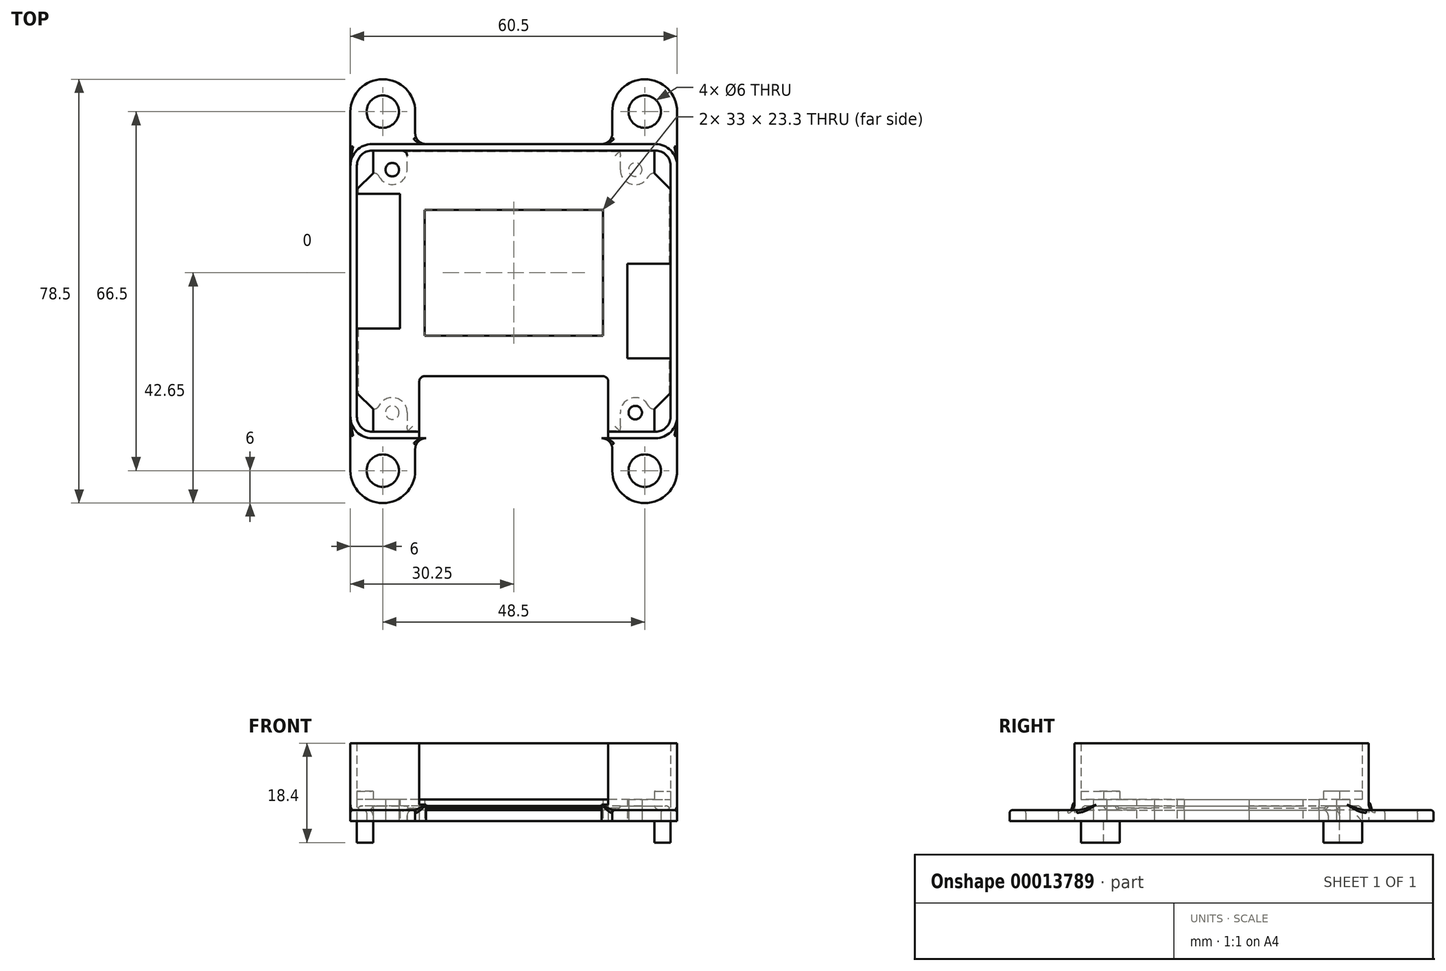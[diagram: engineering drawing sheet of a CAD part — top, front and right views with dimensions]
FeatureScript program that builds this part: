
annotation { "Feature Type Name" : "Feature", "Feature Type Description" : "" }
export const myFeature = defineFeature(function(context is Context, id is Id, definition is map)
    precondition{}
    {
        {
            var Q0;
            Q0=qCreatedBy(makeId("Top.planeOp"),FACE);
            var sketch = newSketch(context, id + "F0", { "sketchPlane" : qUnion([Q0])});
            skLineSegment(sketch, "E0.rect.bottom", {"start": v(26.25, 27.25) * mm, "end": v(-26.25, 27.25) * mm});
            skLineSegment(sketch, "E0.rect.top", {"start": v(26.25, -27.25) * mm, "end": v(-26.25, -27.25) * mm});
            skLineSegment(sketch, "E0.rect.left", {"start": v(30.25, 33.25) * mm, "end": v(30.25, 23.25) * mm});
            skLineSegment(sketch, "E0.rect.right", {"start": v(-30.25, 23.25) * mm, "end": v(-30.25, -23.25) * mm});
            skPoint(sketch, "E0.rect.middle", {"position": v(0, 0) * mm});
            skCircle(sketch, "E1", {"center": v(24.25, 33.25) * mm, "radius": 3 * mm});
            skArc(sketch, "E2.0", {"start": v(30.25, 33.25) * mm, "mid": v(24.25, 39.25) * mm, "end": v(18.25, 33.25) * mm});
            skPoint(sketch, "E3.visualSharp", {"position": v(30.25, 27.25) * mm});
            skArc(sketch, "E3.filletArc", {"start": v(30.25, 23.25) * mm, "mid": v(29.08, 26.08) * mm, "end": v(26.25, 27.25) * mm});
            skPoint(sketch, "E4.visualSharp", {"position": v(-30.25, 27.25) * mm});
            skArc(sketch, "E4.filletArc", {"start": v(-26.25, 27.25) * mm, "mid": v(-29.08, 26.08) * mm, "end": v(-30.25, 23.25) * mm});
            skPoint(sketch, "E5.visualSharp", {"position": v(30.25, -27.25) * mm});
            skArc(sketch, "E5.filletArc", {"start": v(26.25, -27.25) * mm, "mid": v(29.08, -26.08) * mm, "end": v(30.25, -23.25) * mm});
            skPoint(sketch, "E6.visualSharp", {"position": v(-30.25, -27.25) * mm});
            skArc(sketch, "E6.filletArc", {"start": v(-30.25, -23.25) * mm, "mid": v(-29.08, -26.08) * mm, "end": v(-26.25, -27.25) * mm});
            skLineSegment(sketch, "E7", {"start": v(18.25, 33.25) * mm, "end": v(18.25, 27.25) * mm});
            skLineSegment(sketch, "E8", {"start": v(0, 27.25) * mm, "end": v(0, -27.25) * mm, "construction": true});
            skLineSegment(sketch, "E9", {"start": v(-30.25, 0) * mm, "end": v(30.25, 0) * mm, "construction": true});
            skLineSegment(sketch, "E10", {"start": v(30.25, 23.25) * mm, "end": v(30.25, -23.25) * mm});
            skArc(sketch, "E11.0", {"start": v(29.05, 23.25) * mm, "mid": v(28.23, 25.23) * mm, "end": v(26.25, 26.05) * mm});
            skLineSegment(sketch, "E11.1", {"start": v(29.05, 23.25) * mm, "end": v(29.05, -23.25) * mm});
            skArc(sketch, "E11.2", {"start": v(26.25, -26.05) * mm, "mid": v(28.23, -25.23) * mm, "end": v(29.05, -23.25) * mm});
            skLineSegment(sketch, "E11.3", {"start": v(26.25, -26.05) * mm, "end": v(-26.25, -26.05) * mm});
            skArc(sketch, "E11.4", {"start": v(-29.05, -23.25) * mm, "mid": v(-28.23, -25.23) * mm, "end": v(-26.25, -26.05) * mm});
            skLineSegment(sketch, "E11.5", {"start": v(26.25, 26.05) * mm, "end": v(-26.25, 26.05) * mm});
            skLineSegment(sketch, "E11.6", {"start": v(-29.05, 23.25) * mm, "end": v(-29.05, -23.25) * mm});
            skArc(sketch, "E11.7", {"start": v(-26.25, 26.05) * mm, "mid": v(-28.23, 25.23) * mm, "end": v(-29.05, 23.25) * mm});
            skCircle(sketch, "E12", {"center": v(22.5, 22.5) * mm, "radius": 1.25 * mm});
            skArc(sketch, "E13.0", {"start": v(19.75, 22.5) * mm, "mid": v(21.87, 19.82) * mm, "end": v(24.97, 21.28) * mm});
            skLineSegment(sketch, "E14.0.MirrorCS", {"start": v(-18.25, 33.25) * mm, "end": v(-18.25, 27.25) * mm});
            skArc(sketch, "E15.0.MirrorC", {"start": v(-30.25, 33.25) * mm, "mid": v(-24.25, 39.25) * mm, "end": v(-18.25, 33.25) * mm});
            skCircle(sketch, "E16.0.MirrorC", {"center": v(-24.25, 33.25) * mm, "radius": 3 * mm});
            skLineSegment(sketch, "E17.0.MirrorCS", {"start": v(-30.25, 33.25) * mm, "end": v(-30.25, 23.25) * mm});
            skLineSegment(sketch, "E18.0.MirrorCS", {"start": v(-30.25, -33.25) * mm, "end": v(-30.25, -23.25) * mm});
            skLineSegment(sketch, "E19.0.MirrorCS", {"start": v(-18.25, -33.25) * mm, "end": v(-18.25, -27.25) * mm});
            skArc(sketch, "E20.0.MirrorC", {"start": v(-30.25, -33.25) * mm, "mid": v(-24.25, -39.25) * mm, "end": v(-18.25, -33.25) * mm});
            skCircle(sketch, "E21.0.MirrorC", {"center": v(-24.25, -33.25) * mm, "radius": 3 * mm});
            skLineSegment(sketch, "E22.0.MirrorCS", {"start": v(18.25, -33.25) * mm, "end": v(18.25, -27.25) * mm});
            skLineSegment(sketch, "E23.0.MirrorCS", {"start": v(30.25, -33.25) * mm, "end": v(30.25, -23.25) * mm});
            skArc(sketch, "E24.0.MirrorC", {"start": v(30.25, -33.25) * mm, "mid": v(24.25, -39.25) * mm, "end": v(18.25, -33.25) * mm});
            skCircle(sketch, "E25.0.MirrorC", {"center": v(24.25, -33.25) * mm, "radius": 3 * mm});
            skLineSegment(sketch, "E26", {"start": v(26.05, 26.05) * mm, "end": v(26.05, 21.84) * mm});
            skLineSegment(sketch, "E27", {"start": v(26.05, 21.84) * mm, "end": v(29.05, 18.84) * mm});
            skLineSegment(sketch, "E28", {"start": v(19.75, 22.5) * mm, "end": v(19.75, 26.05) * mm});
            skCircle(sketch, "E29.0.MirrorC", {"center": v(-22.5, 22.5) * mm, "radius": 1.25 * mm});
            skLineSegment(sketch, "E30", {"start": v(26.05, 21.84) * mm, "end": v(25.86, 21.84) * mm});
            skPoint(sketch, "E31.visualSharp", {"position": v(25.17, 21.84) * mm});
            skArc(sketch, "E31.filletArc", {"start": v(25.86, 21.84) * mm, "mid": v(25.33, 21.69) * mm, "end": v(24.97, 21.28) * mm});
            skLineSegment(sketch, "E32.0.MirrorCS", {"start": v(-19.75, 22.5) * mm, "end": v(-19.75, 26.05) * mm});
            skArc(sketch, "E33.0.MirrorCS", {"start": v(-19.75, 22.5) * mm, "mid": v(-21.87, 19.82) * mm, "end": v(-24.97, 21.28) * mm});
            skArc(sketch, "E34.0.MirrorCS", {"start": v(-25.86, 21.84) * mm, "mid": v(-25.33, 21.69) * mm, "end": v(-24.97, 21.28) * mm});
            skLineSegment(sketch, "E35.0.MirrorCS", {"start": v(-26.05, 21.84) * mm, "end": v(-25.86, 21.84) * mm});
            skLineSegment(sketch, "E36.0.MirrorCS", {"start": v(-26.05, 21.84) * mm, "end": v(-29.05, 18.84) * mm});
            skLineSegment(sketch, "E37.0.MirrorCS", {"start": v(-26.05, 26.05) * mm, "end": v(-26.05, 21.84) * mm});
            skLineSegment(sketch, "E38.0.MirrorCS", {"start": v(26.05, -21.84) * mm, "end": v(25.86, -21.84) * mm});
            skArc(sketch, "E38.1.MirrorCS", {"start": v(25.86, -21.84) * mm, "mid": v(25.33, -21.69) * mm, "end": v(24.97, -21.28) * mm});
            skLineSegment(sketch, "E38.2.MirrorCS", {"start": v(26.05, -21.84) * mm, "end": v(29.05, -18.84) * mm});
            skArc(sketch, "E38.3.MirrorCS", {"start": v(19.75, -22.5) * mm, "mid": v(21.87, -19.82) * mm, "end": v(24.97, -21.28) * mm});
            skLineSegment(sketch, "E38.4.MirrorCS", {"start": v(19.75, -22.5) * mm, "end": v(19.75, -26.05) * mm});
            skLineSegment(sketch, "E38.5.MirrorCS", {"start": v(26.05, -26.05) * mm, "end": v(26.05, -21.84) * mm});
            skCircle(sketch, "E38.6.MirrorC", {"center": v(22.5, -22.5) * mm, "radius": 1.25 * mm});
            skLineSegment(sketch, "E38.7.MirrorCS", {"start": v(-26.05, -21.84) * mm, "end": v(-25.86, -21.84) * mm});
            skArc(sketch, "E38.8.MirrorCS", {"start": v(-25.86, -21.84) * mm, "mid": v(-25.33, -21.69) * mm, "end": v(-24.97, -21.28) * mm});
            skArc(sketch, "E38.9.MirrorCS", {"start": v(-19.75, -22.5) * mm, "mid": v(-21.87, -19.82) * mm, "end": v(-24.97, -21.28) * mm});
            skLineSegment(sketch, "E38.10.MirrorCS", {"start": v(-26.05, -21.84) * mm, "end": v(-29.05, -18.84) * mm});
            skLineSegment(sketch, "E38.12.MirrorCS", {"start": v(-26.05, -26.05) * mm, "end": v(-26.05, -21.84) * mm});
            skLineSegment(sketch, "E38.13.MirrorCS", {"start": v(-19.75, -22.5) * mm, "end": v(-19.75, -26.05) * mm});
            skCircle(sketch, "E39.0.MirrorC", {"center": v(-22.5, -22.5) * mm, "radius": 1.25 * mm});
            skSolve(sketch);
        }
        {
            var Q0;
            {var subQ1=sQuery(id+"F0.wireOp",EDGE,"E4.filletArc");Q0=makeQuery(id+"F0.imprint","IMPRINT",FACE,{"disambiguationData":[TD([[makeQuery(id+"F0.imprint","IMPRINT",EDGE,{"derivedFrom":subQ1}),-1.0]])]});}
            var Q1;
            {var subQ1=sQuery(id+"F0.wireOp",EDGE,"E4.filletArc");Q1=makeQuery(id+"F0.imprint","IMPRINT",FACE,{"disambiguationData":[TD([[makeQuery(id+"F0.imprint","IMPRINT",EDGE,{"derivedFrom":subQ1}),-1.0]])]});}
            var Q2;
            {var subQ1=sQuery(id+"F0.wireOp",EDGE,"E4.filletArc");Q2=makeQuery(id+"F0.imprint","IMPRINT",FACE,{"disambiguationData":[TD([[makeQuery(id+"F0.imprint","IMPRINT",EDGE,{"derivedFrom":subQ1}),-1.0]])]});}
            var Q3;
            Q3=makeQuery(id+"F0.imprint","IMPRINT",FACE,{"disambiguationData":[TD([[makeQuery(id+"F0.imprint","IMPRINT",EDGE,{"derivedFrom":sQuery(id+"F0.wireOp",EDGE,"E0.rect.left")}),-1.0]])]});
            var Q4;
            Q4=makeQuery(id+"F0.imprint","IMPRINT",FACE,{"disambiguationData":[TD([[makeQuery(id+"F0.imprint","IMPRINT",EDGE,{"derivedFrom":sQuery(id+"F0.wireOp",EDGE,"E0.rect.left")}),-1.0]])]});
            var Q5;
            Q5=makeQuery(id+"F0.imprint","IMPRINT",FACE,{"disambiguationData":[TD([[makeQuery(id+"F0.imprint","IMPRINT",EDGE,{"derivedFrom":sQuery(id+"F0.wireOp",EDGE,"E0.rect.left")}),-1.0]])]});
            var Q6;
            Q6=makeQuery(id+"F0.imprint","IMPRINT",FACE,{"disambiguationData":[TD([[makeQuery(id+"F0.imprint","IMPRINT",EDGE,{"derivedFrom":sQuery(id+"F0.wireOp",EDGE,"E0.rect.right")}),1.0]])]});
            var Q7;
            {var subQ3=sQuery(id+"F0.wireOp",EDGE,"E11.0");Q7=makeQuery(id+"F0.imprint","IMPRINT",FACE,{"disambiguationData":[TD([[makeQuery(id+"F0.imprint","IMPRINT",EDGE,{"derivedFrom":subQ3}),1.0]])]});}
            var Q8;
            {var subQ1=sQuery(id+"F0.wireOp",EDGE,"E5.filletArc");Q8=makeQuery(id+"F0.imprint","IMPRINT",FACE,{"disambiguationData":[TD([[makeQuery(id+"F0.imprint","IMPRINT",EDGE,{"derivedFrom":subQ1}),-1.0]])]});}
            var Q9;
            {var subQ1=sQuery(id+"F0.wireOp",EDGE,"E5.filletArc");Q9=makeQuery(id+"F0.imprint","IMPRINT",FACE,{"disambiguationData":[TD([[makeQuery(id+"F0.imprint","IMPRINT",EDGE,{"derivedFrom":subQ1}),-1.0]])]});}
            var Q10;
            {var subQ1=sQuery(id+"F0.wireOp",EDGE,"E5.filletArc");Q10=makeQuery(id+"F0.imprint","IMPRINT",FACE,{"disambiguationData":[TD([[makeQuery(id+"F0.imprint","IMPRINT",EDGE,{"derivedFrom":subQ1}),-1.0]])]});}
            var Q11;
            {var subQ1=sQuery(id+"F0.wireOp",EDGE,"E6.filletArc");Q11=makeQuery(id+"F0.imprint","IMPRINT",FACE,{"disambiguationData":[TD([[makeQuery(id+"F0.imprint","IMPRINT",EDGE,{"derivedFrom":subQ1}),-1.0]])]});}
            var Q12;
            {var subQ1=sQuery(id+"F0.wireOp",EDGE,"E6.filletArc");Q12=makeQuery(id+"F0.imprint","IMPRINT",FACE,{"disambiguationData":[TD([[makeQuery(id+"F0.imprint","IMPRINT",EDGE,{"derivedFrom":subQ1}),-1.0]])]});}
            var Q13;
            {var subQ1=sQuery(id+"F0.wireOp",EDGE,"E6.filletArc");Q13=makeQuery(id+"F0.imprint","IMPRINT",FACE,{"disambiguationData":[TD([[makeQuery(id+"F0.imprint","IMPRINT",EDGE,{"derivedFrom":subQ1}),-1.0]])]});}
            var Q14;
            Q14=makeQuery(id+"F0.imprint","IMPRINT",FACE,{"disambiguationData":[TD([[makeQuery(id+"F0.imprint","IMPRINT",EDGE,{"derivedFrom":sQuery(id+"F0.wireOp",EDGE,"4b78b91a-cd40-4b56-b6ec-8fa9bed8e85b.0.MirrorC")}),1.0]])]});
            var Q15;
            Q15=makeQuery(id+"F0.imprint","IMPRINT",FACE,{"disambiguationData":[TD([[makeQuery(id+"F0.imprint","IMPRINT",EDGE,{"derivedFrom":sQuery(id+"F0.wireOp",EDGE,"aa0879d5-27ab-45ad-85e8-511e2dc1aff2.0.MirrorC")}),-1.0]])]});
            var Q16;
            Q16=makeQuery(id+"F0.imprint","IMPRINT",FACE,{"disambiguationData":[TD([[makeQuery(id+"F0.imprint","IMPRINT",EDGE,{"derivedFrom":sQuery(id+"F0.wireOp",EDGE,"160e8c58-b794-47d6-928c-0b94daf968f9.0.MirrorC")}),1.0]])]});
            var Q17;
            Q17=makeQuery(id+"F0.imprint","IMPRINT",FACE,{"disambiguationData":[TD([[makeQuery(id+"F0.imprint","IMPRINT",EDGE,{"derivedFrom":sQuery(id+"F0.wireOp",EDGE,"E12")}),-1.0]])]});
            var Q18;
            {var subQ2=sQuery(id+"F0.wireOp",EDGE,"E11.7");Q18=makeQuery(id+"F0.imprint","IMPRINT",FACE,{"disambiguationData":[TD([[makeQuery(id+"F0.imprint","IMPRINT",EDGE,{"derivedFrom":subQ2}),1.0]])]});}
            var Q19;
            {var subQ3=sQuery(id+"F0.wireOp",EDGE,"E11.4");Q19=makeQuery(id+"F0.imprint","IMPRINT",FACE,{"disambiguationData":[TD([[makeQuery(id+"F0.imprint","IMPRINT",EDGE,{"derivedFrom":subQ3}),1.0]])]});}
            var Q20;
            {var subQ3=sQuery(id+"F0.wireOp",EDGE,"E11.2");Q20=makeQuery(id+"F0.imprint","IMPRINT",FACE,{"disambiguationData":[TD([[makeQuery(id+"F0.imprint","IMPRINT",EDGE,{"derivedFrom":subQ3}),1.0]])]});}
            var Q21;
            {var subQ3=sQuery(id+"F0.wireOp",EDGE,"E11.2");var subQ8=sQuery(id+"F0.wireOp",EDGE,"E11.4");Q21=qUnion([makeQuery(id+"F0.imprint","IMPRINT",FACE,{"disambiguationData":[TD([[makeQuery(id+"F0.imprint","IMPRINT",EDGE,{"derivedFrom":subQ3}),1.0]])]}),makeQuery(id+"F0.imprint","IMPRINT",FACE,{"disambiguationData":[TD([[makeQuery(id+"F0.imprint","IMPRINT",EDGE,{"derivedFrom":subQ8}),1.0]])]})]);}
            var Q22;
            Q22=makeQuery(id+"F0.imprint","IMPRINT",FACE,{"disambiguationData":[TD([[makeQuery(id+"F0.imprint","IMPRINT",EDGE,{"derivedFrom":sQuery(id+"F0.wireOp",EDGE,"E13.0")}),-1.0]])]});
            var Q23;
            Q23=makeQuery(id+"F0.imprint","IMPRINT",FACE,{"disambiguationData":[TD([[makeQuery(id+"F0.imprint","IMPRINT",EDGE,{"derivedFrom":sQuery(id+"F0.wireOp",EDGE,"E29.0.MirrorC")}),1.0]])]});
            var Q24;
            Q24=makeQuery(id+"F0.imprint","IMPRINT",FACE,{"disambiguationData":[TD([[makeQuery(id+"F0.imprint","IMPRINT",EDGE,{"derivedFrom":sQuery(id+"F0.wireOp",EDGE,"E38.0.MirrorCS")}),1.0]])]});
            var Q25;
            Q25=makeQuery(id+"F0.imprint","IMPRINT",FACE,{"disambiguationData":[TD([[makeQuery(id+"F0.imprint","IMPRINT",EDGE,{"derivedFrom":sQuery(id+"F0.wireOp",EDGE,"E38.7.MirrorCS")}),-1.0]])]});
            extrude(context, id + "F1", {"entities" : qUnion([Q0, Q1, Q2, Q3, Q4, Q5, Q6, Q7, Q8, Q9, Q10, Q11, Q12, Q13, Q14, Q15, Q16, Q17, Q18, Q19, Q20, Q21, Q22, Q23, Q24, Q25]), "depth" : 2 * mm});
        }
        {
            var Q0;
            Q0=makeQuery(id+"F0.imprint","IMPRINT",FACE,{"disambiguationData":[TD([[makeQuery(id+"F0.imprint","IMPRINT",EDGE,{"derivedFrom":sQuery(id+"F0.wireOp",EDGE,"E0.rect.right")}),1.0]])]});
            extrude(context, id + "F2", {"entities" : qUnion([Q0]), "operationType" : NewBodyOperationType.ADD, "depth" : 14.4 * mm});
        }
        {
            var Q0;
            Q0=makeQuery(id+"F0.imprint","IMPRINT",FACE,{"disambiguationData":[TD([[makeQuery(id+"F0.imprint","IMPRINT",EDGE,{"derivedFrom":sQuery(id+"F0.wireOp",EDGE,"E38.0.MirrorCS")}),1.0]])]});
            var Q1;
            Q1=makeQuery(id+"F0.imprint","IMPRINT",FACE,{"disambiguationData":[TD([[makeQuery(id+"F0.imprint","IMPRINT",EDGE,{"derivedFrom":sQuery(id+"F0.wireOp",EDGE,"E38.7.MirrorCS")}),-1.0]])]});
            var Q2;
            Q2=makeQuery(id+"F0.imprint","IMPRINT",FACE,{"disambiguationData":[TD([[makeQuery(id+"F0.imprint","IMPRINT",EDGE,{"derivedFrom":sQuery(id+"F0.wireOp",EDGE,"E29.0.MirrorC")}),1.0]])]});
            var Q3;
            Q3=makeQuery(id+"F0.imprint","IMPRINT",FACE,{"disambiguationData":[TD([[makeQuery(id+"F0.imprint","IMPRINT",EDGE,{"derivedFrom":sQuery(id+"F0.wireOp",EDGE,"E12")}),-1.0]])]});
            extrude(context, id + "F3", {"entities" : qUnion([Q0, Q1, Q2, Q3]), "operationType" : NewBodyOperationType.ADD, "depth" : 4 * mm});
        }
        {
            var Q0;
            {var subQ0=sQuery(id+"F0.wireOp",EDGE,"E0.rect.top");Q0=makeQuery(id+"F2.boolean.opBoolean","MERGE",FACE,{"derivedFrom":[makeQuery(id+"F1.opExtrude","SWEPT_FACE",FACE,{"disambiguationData":[OSD([subQ0])]}),makeQuery(id+"F2.opExtrude","SWEPT_FACE",FACE,{"disambiguationData":[OSD([subQ0])]})]});}
            var sketch = newSketch(context, id + "F4", { "sketchPlane" : qUnion([Q0])});
            skPoint(sketch, "E40", {"position": v(0, 0) * mm});
            skLineSegment(sketch, "E41", {"start": v(0, 14.4) * mm, "end": v(0, 0) * mm, "construction": true});
            skLineSegment(sketch, "E42", {"start": v(-15.5, 6.4) * mm, "end": v(15.5, 6.4) * mm});
            skPoint(sketch, "E43", {"position": v(0, 6.4) * mm});
            skLineSegment(sketch, "E44", {"start": v(-17.5, 8.4) * mm, "end": v(-17.5, 14.4) * mm});
            skLineSegment(sketch, "E45", {"start": v(17.5, 8.4) * mm, "end": v(17.5, 14.4) * mm});
            skPoint(sketch, "E46.visualSharp", {"position": v(-17.5, 6.4) * mm});
            skArc(sketch, "E46.filletArc", {"start": v(-17.5, 8.4) * mm, "mid": v(-16.91, 6.99) * mm, "end": v(-15.5, 6.4) * mm});
            skPoint(sketch, "E47.visualSharp", {"position": v(17.5, 6.4) * mm});
            skArc(sketch, "E47.filletArc", {"start": v(15.5, 6.4) * mm, "mid": v(16.91, 6.99) * mm, "end": v(17.5, 8.4) * mm});
            skSolve(sketch);
        }
        {
            var Q0;
            Q0=makeQuery(id+"F2.boolean.opBoolean","INTERSECT",EDGE,{"derivedFrom":[makeQuery(id+"F1.opExtrude","CAP_FACE",FACE,{"disambiguationData":[OSD([sQuery(id+"F0.wireOp",EDGE,"E0.rect.bottom"),sQuery(id+"F0.wireOp",EDGE,"E0.rect.top"),sQuery(id+"F0.wireOp",EDGE,"E0.rect.left"),sQuery(id+"F0.wireOp",EDGE,"E0.rect.right"),sQuery(id+"F0.wireOp",EDGE,"E1"),sQuery(id+"F0.wireOp",EDGE,"E2.0"),sQuery(id+"F0.wireOp",EDGE,"E7"),sQuery(id+"F0.wireOp",EDGE,"E10"),sQuery(id+"F0.wireOp",EDGE,"E12"),sQuery(id+"F0.wireOp",EDGE,"E14.0.MirrorCS"),sQuery(id+"F0.wireOp",EDGE,"E15.0.MirrorC"),sQuery(id+"F0.wireOp",EDGE,"E16.0.MirrorC"),sQuery(id+"F0.wireOp",EDGE,"E17.0.MirrorCS"),sQuery(id+"F0.wireOp",EDGE,"E18.0.MirrorCS"),sQuery(id+"F0.wireOp",EDGE,"E19.0.MirrorCS"),sQuery(id+"F0.wireOp",EDGE,"E20.0.MirrorC"),sQuery(id+"F0.wireOp",EDGE,"E21.0.MirrorC"),sQuery(id+"F0.wireOp",EDGE,"E22.0.MirrorCS"),sQuery(id+"F0.wireOp",EDGE,"E23.0.MirrorCS"),sQuery(id+"F0.wireOp",EDGE,"E24.0.MirrorC"),sQuery(id+"F0.wireOp",EDGE,"E25.0.MirrorC"),sQuery(id+"F0.wireOp",EDGE,"E29.0.MirrorC"),sQuery(id+"F0.wireOp",EDGE,"E38.6.MirrorC"),sQuery(id+"F0.wireOp",EDGE,"E39.0.MirrorC")])],"isStart":false}),makeQuery(id+"F2.opExtrude","SWEPT_FACE",FACE,{"disambiguationData":[OSD([sQuery(id+"F0.wireOp",EDGE,"E6.filletArc")])]})]});
            var Q1;
            Q1=makeQuery(id+"F2.boolean.opBoolean","INTERSECT",EDGE,{"derivedFrom":[makeQuery(id+"F1.opExtrude","CAP_FACE",FACE,{"disambiguationData":[OSD([sQuery(id+"F0.wireOp",EDGE,"E0.rect.bottom"),sQuery(id+"F0.wireOp",EDGE,"E0.rect.top"),sQuery(id+"F0.wireOp",EDGE,"E0.rect.left"),sQuery(id+"F0.wireOp",EDGE,"E0.rect.right"),sQuery(id+"F0.wireOp",EDGE,"E1"),sQuery(id+"F0.wireOp",EDGE,"E2.0"),sQuery(id+"F0.wireOp",EDGE,"E7"),sQuery(id+"F0.wireOp",EDGE,"E10"),sQuery(id+"F0.wireOp",EDGE,"E12"),sQuery(id+"F0.wireOp",EDGE,"E14.0.MirrorCS"),sQuery(id+"F0.wireOp",EDGE,"E15.0.MirrorC"),sQuery(id+"F0.wireOp",EDGE,"E16.0.MirrorC"),sQuery(id+"F0.wireOp",EDGE,"E17.0.MirrorCS"),sQuery(id+"F0.wireOp",EDGE,"E18.0.MirrorCS"),sQuery(id+"F0.wireOp",EDGE,"E19.0.MirrorCS"),sQuery(id+"F0.wireOp",EDGE,"E20.0.MirrorC"),sQuery(id+"F0.wireOp",EDGE,"E21.0.MirrorC"),sQuery(id+"F0.wireOp",EDGE,"E22.0.MirrorCS"),sQuery(id+"F0.wireOp",EDGE,"E23.0.MirrorCS"),sQuery(id+"F0.wireOp",EDGE,"E24.0.MirrorC"),sQuery(id+"F0.wireOp",EDGE,"E25.0.MirrorC"),sQuery(id+"F0.wireOp",EDGE,"E29.0.MirrorC"),sQuery(id+"F0.wireOp",EDGE,"E38.6.MirrorC"),sQuery(id+"F0.wireOp",EDGE,"E39.0.MirrorC")])],"isStart":false}),makeQuery(id+"F2.opExtrude","SWEPT_FACE",FACE,{"disambiguationData":[OSD([sQuery(id+"F0.wireOp",EDGE,"E5.filletArc")])]})]});
            var Q2;
            Q2=makeQuery(id+"F2.boolean.opBoolean","INTERSECT",EDGE,{"derivedFrom":[makeQuery(id+"F1.opExtrude","CAP_FACE",FACE,{"disambiguationData":[OSD([sQuery(id+"F0.wireOp",EDGE,"E0.rect.bottom"),sQuery(id+"F0.wireOp",EDGE,"E0.rect.top"),sQuery(id+"F0.wireOp",EDGE,"E0.rect.left"),sQuery(id+"F0.wireOp",EDGE,"E0.rect.right"),sQuery(id+"F0.wireOp",EDGE,"E1"),sQuery(id+"F0.wireOp",EDGE,"E2.0"),sQuery(id+"F0.wireOp",EDGE,"E7"),sQuery(id+"F0.wireOp",EDGE,"E10"),sQuery(id+"F0.wireOp",EDGE,"E12"),sQuery(id+"F0.wireOp",EDGE,"E14.0.MirrorCS"),sQuery(id+"F0.wireOp",EDGE,"E15.0.MirrorC"),sQuery(id+"F0.wireOp",EDGE,"E16.0.MirrorC"),sQuery(id+"F0.wireOp",EDGE,"E17.0.MirrorCS"),sQuery(id+"F0.wireOp",EDGE,"E18.0.MirrorCS"),sQuery(id+"F0.wireOp",EDGE,"E19.0.MirrorCS"),sQuery(id+"F0.wireOp",EDGE,"E20.0.MirrorC"),sQuery(id+"F0.wireOp",EDGE,"E21.0.MirrorC"),sQuery(id+"F0.wireOp",EDGE,"E22.0.MirrorCS"),sQuery(id+"F0.wireOp",EDGE,"E23.0.MirrorCS"),sQuery(id+"F0.wireOp",EDGE,"E24.0.MirrorC"),sQuery(id+"F0.wireOp",EDGE,"E25.0.MirrorC"),sQuery(id+"F0.wireOp",EDGE,"E29.0.MirrorC"),sQuery(id+"F0.wireOp",EDGE,"E38.6.MirrorC"),sQuery(id+"F0.wireOp",EDGE,"E39.0.MirrorC")])],"isStart":false}),makeQuery(id+"F2.opExtrude","SWEPT_FACE",FACE,{"disambiguationData":[OSD([sQuery(id+"F0.wireOp",EDGE,"E3.filletArc")])]})]});
            var Q3;
            Q3=makeQuery(id+"F2.boolean.opBoolean","INTERSECT",EDGE,{"derivedFrom":[makeQuery(id+"F1.opExtrude","CAP_FACE",FACE,{"disambiguationData":[OSD([sQuery(id+"F0.wireOp",EDGE,"E0.rect.bottom"),sQuery(id+"F0.wireOp",EDGE,"E0.rect.top"),sQuery(id+"F0.wireOp",EDGE,"E0.rect.left"),sQuery(id+"F0.wireOp",EDGE,"E0.rect.right"),sQuery(id+"F0.wireOp",EDGE,"E1"),sQuery(id+"F0.wireOp",EDGE,"E2.0"),sQuery(id+"F0.wireOp",EDGE,"E7"),sQuery(id+"F0.wireOp",EDGE,"E10"),sQuery(id+"F0.wireOp",EDGE,"E12"),sQuery(id+"F0.wireOp",EDGE,"E14.0.MirrorCS"),sQuery(id+"F0.wireOp",EDGE,"E15.0.MirrorC"),sQuery(id+"F0.wireOp",EDGE,"E16.0.MirrorC"),sQuery(id+"F0.wireOp",EDGE,"E17.0.MirrorCS"),sQuery(id+"F0.wireOp",EDGE,"E18.0.MirrorCS"),sQuery(id+"F0.wireOp",EDGE,"E19.0.MirrorCS"),sQuery(id+"F0.wireOp",EDGE,"E20.0.MirrorC"),sQuery(id+"F0.wireOp",EDGE,"E21.0.MirrorC"),sQuery(id+"F0.wireOp",EDGE,"E22.0.MirrorCS"),sQuery(id+"F0.wireOp",EDGE,"E23.0.MirrorCS"),sQuery(id+"F0.wireOp",EDGE,"E24.0.MirrorC"),sQuery(id+"F0.wireOp",EDGE,"E25.0.MirrorC"),sQuery(id+"F0.wireOp",EDGE,"E29.0.MirrorC"),sQuery(id+"F0.wireOp",EDGE,"E38.6.MirrorC"),sQuery(id+"F0.wireOp",EDGE,"E39.0.MirrorC")])],"isStart":false}),makeQuery(id+"F2.opExtrude","SWEPT_FACE",FACE,{"disambiguationData":[OSD([sQuery(id+"F0.wireOp",EDGE,"E4.filletArc")])]})]});
            fillet(context, id + "F5", {"entities" : qUnion([Q0, Q1, Q2, Q3]), "radius" : 1 * mm, "tangentPropagation" : true, "allowEdgeOverflow" : false});
        }
        {
            var Q0;
            Q0=makeQuery(id+"F1.opExtrude","SWEPT_EDGE",EDGE,{"disambiguationData":[OSD([sQuery(id+"F0.wireOp",EDGE,"E0.rect.top"),sQuery(id+"F0.wireOp",EDGE,"E19.0.MirrorCS")])]});
            var Q1;
            Q1=makeQuery(id+"F1.opExtrude","SWEPT_EDGE",EDGE,{"disambiguationData":[OSD([sQuery(id+"F0.wireOp",EDGE,"E0.rect.top"),sQuery(id+"F0.wireOp",EDGE,"E22.0.MirrorCS")])]});
            var Q2;
            Q2=makeQuery(id+"F1.opExtrude","SWEPT_EDGE",EDGE,{"disambiguationData":[OSD([sQuery(id+"F0.wireOp",EDGE,"E0.rect.bottom"),sQuery(id+"F0.wireOp",EDGE,"E7")])]});
            var Q3;
            Q3=makeQuery(id+"F1.opExtrude","SWEPT_EDGE",EDGE,{"disambiguationData":[OSD([sQuery(id+"F0.wireOp",EDGE,"E0.rect.bottom"),sQuery(id+"F0.wireOp",EDGE,"E14.0.MirrorCS")])]});
            fillet(context, id + "F6", {"entities" : qUnion([Q0, Q1, Q2, Q3]), "radius" : 2 * mm, "tangentPropagation" : true, "allowEdgeOverflow" : false});
        }
        {
            var Q0;
            Q0=makeQuery(id+"F4.imprint","IMPRINT",FACE,{"disambiguationData":[TD([[makeQuery(id+"F4.imprint","IMPRINT",EDGE,{"derivedFrom":sQuery(id+"F4.wireOp",EDGE,"E42")}),1.0]])]});
            extrude(context, id + "F7", {"entities" : qUnion([Q0]), "operationType" : NewBodyOperationType.REMOVE, "endBound" : BoundingType.UP_TO_NEXT, "oppositeDirection" : true, "depth" : 25 * mm});
        }
        {
            var Q0;
            {var subQ3=sQuery(id+"F0.wireOp",EDGE,"E11.2");Q0=makeQuery(id+"F0.imprint","IMPRINT",FACE,{"disambiguationData":[TD([[makeQuery(id+"F0.imprint","IMPRINT",EDGE,{"derivedFrom":subQ3}),1.0]])]});}
            var Q1;
            {var subQ3=sQuery(id+"F0.wireOp",EDGE,"E11.4");Q1=makeQuery(id+"F0.imprint","IMPRINT",FACE,{"disambiguationData":[TD([[makeQuery(id+"F0.imprint","IMPRINT",EDGE,{"derivedFrom":subQ3}),1.0]])]});}
            var Q2;
            {var subQ2=sQuery(id+"F0.wireOp",EDGE,"E11.7");Q2=makeQuery(id+"F0.imprint","IMPRINT",FACE,{"disambiguationData":[TD([[makeQuery(id+"F0.imprint","IMPRINT",EDGE,{"derivedFrom":subQ2}),1.0]])]});}
            var Q3;
            {var subQ3=sQuery(id+"F0.wireOp",EDGE,"E11.0");Q3=makeQuery(id+"F0.imprint","IMPRINT",FACE,{"disambiguationData":[TD([[makeQuery(id+"F0.imprint","IMPRINT",EDGE,{"derivedFrom":subQ3}),1.0]])]});}
            extrude(context, id + "F8", {"entities" : qUnion([Q0, Q1, Q2, Q3]), "depth" : 5.5 * mm});
        }
        {
            var Q0;
            {var subQ3=sQuery(id+"F0.wireOp",EDGE,"E11.2");Q0=makeQuery(id+"F0.imprint","IMPRINT",FACE,{"disambiguationData":[TD([[makeQuery(id+"F0.imprint","IMPRINT",EDGE,{"derivedFrom":subQ3}),1.0]])]});}
            var Q1;
            {var subQ3=sQuery(id+"F0.wireOp",EDGE,"E11.4");Q1=makeQuery(id+"F0.imprint","IMPRINT",FACE,{"disambiguationData":[TD([[makeQuery(id+"F0.imprint","IMPRINT",EDGE,{"derivedFrom":subQ3}),1.0]])]});}
            var Q2;
            {var subQ3=sQuery(id+"F0.wireOp",EDGE,"E11.0");Q2=makeQuery(id+"F0.imprint","IMPRINT",FACE,{"disambiguationData":[TD([[makeQuery(id+"F0.imprint","IMPRINT",EDGE,{"derivedFrom":subQ3}),1.0]])]});}
            var Q3;
            {var subQ2=sQuery(id+"F0.wireOp",EDGE,"E11.7");Q3=makeQuery(id+"F0.imprint","IMPRINT",FACE,{"disambiguationData":[TD([[makeQuery(id+"F0.imprint","IMPRINT",EDGE,{"derivedFrom":subQ2}),1.0]])]});}
            extrude(context, id + "F9", {"entities" : qUnion([Q0, Q1, Q2, Q3]), "operationType" : NewBodyOperationType.ADD, "depth" : 5.5 * mm});
        }
        {
            var Q0;
            Q0=makeQuery(id+"F1.opExtrude","CAP_EDGE",EDGE,{"disambiguationData":[OSD([sQuery(id+"F0.wireOp",EDGE,"E21.0.MirrorC")])],"isStart":false});
            var Q1;
            Q1=makeQuery(id+"F1.opExtrude","CAP_EDGE",EDGE,{"disambiguationData":[OSD([sQuery(id+"F0.wireOp",EDGE,"E25.0.MirrorC")])],"isStart":false});
            var Q2;
            Q2=makeQuery(id+"F1.opExtrude","CAP_EDGE",EDGE,{"disambiguationData":[OSD([sQuery(id+"F0.wireOp",EDGE,"E16.0.MirrorC")])],"isStart":false});
            var Q3;
            Q3=makeQuery(id+"F1.opExtrude","CAP_EDGE",EDGE,{"disambiguationData":[OSD([sQuery(id+"F0.wireOp",EDGE,"E1")])],"isStart":false});
            var Q4;
            Q4=makeQuery(id+"F1.opExtrude","CAP_EDGE",EDGE,{"disambiguationData":[OSD([sQuery(id+"F0.wireOp",EDGE,"E20.0.MirrorC")])],"isStart":false});
            var Q5;
            Q5=makeQuery(id+"F1.opExtrude","CAP_EDGE",EDGE,{"disambiguationData":[OSD([sQuery(id+"F0.wireOp",EDGE,"E24.0.MirrorC")])],"isStart":false});
            var Q6;
            Q6=makeQuery(id+"F1.opExtrude","CAP_EDGE",EDGE,{"disambiguationData":[OSD([sQuery(id+"F0.wireOp",EDGE,"E2.0")])],"isStart":false});
            var Q7;
            Q7=makeQuery(id+"F1.opExtrude","CAP_EDGE",EDGE,{"disambiguationData":[OSD([sQuery(id+"F0.wireOp",EDGE,"E15.0.MirrorC")])],"isStart":false});
            fillet(context, id + "F10", {"entities" : qUnion([Q0, Q1, Q2, Q3, Q4, Q5, Q6, Q7]), "radius" : 0.5 * mm, "tangentPropagation" : true, "allowEdgeOverflow" : false});
        }
        {
            var Q0;
            Q0=makeQuery(id+"F1.opExtrude","CAP_EDGE",EDGE,{"disambiguationData":[OSD([sQuery(id+"F0.wireOp",EDGE,"E38.3.MirrorCS")])],"isStart":false});
            var Q1;
            {var subQ0=makeQuery(id+"F1.opExtrude","CAP_FACE",FACE,{"disambiguationData":[OSD([sQuery(id+"F0.wireOp",EDGE,"E0.rect.bottom"),sQuery(id+"F0.wireOp",EDGE,"E0.rect.top"),sQuery(id+"F0.wireOp",EDGE,"E0.rect.left"),sQuery(id+"F0.wireOp",EDGE,"E0.rect.right"),sQuery(id+"F0.wireOp",EDGE,"E1"),sQuery(id+"F0.wireOp",EDGE,"E2.0"),sQuery(id+"F0.wireOp",EDGE,"E7"),sQuery(id+"F0.wireOp",EDGE,"E10"),sQuery(id+"F0.wireOp",EDGE,"E12"),sQuery(id+"F0.wireOp",EDGE,"E14.0.MirrorCS"),sQuery(id+"F0.wireOp",EDGE,"E15.0.MirrorC"),sQuery(id+"F0.wireOp",EDGE,"E16.0.MirrorC"),sQuery(id+"F0.wireOp",EDGE,"E17.0.MirrorCS"),sQuery(id+"F0.wireOp",EDGE,"E18.0.MirrorCS"),sQuery(id+"F0.wireOp",EDGE,"E19.0.MirrorCS"),sQuery(id+"F0.wireOp",EDGE,"E20.0.MirrorC"),sQuery(id+"F0.wireOp",EDGE,"E21.0.MirrorC"),sQuery(id+"F0.wireOp",EDGE,"E22.0.MirrorCS"),sQuery(id+"F0.wireOp",EDGE,"E23.0.MirrorCS"),sQuery(id+"F0.wireOp",EDGE,"E24.0.MirrorC"),sQuery(id+"F0.wireOp",EDGE,"E25.0.MirrorC"),sQuery(id+"F0.wireOp",EDGE,"E29.0.MirrorC"),sQuery(id+"F0.wireOp",EDGE,"E38.6.MirrorC"),sQuery(id+"F0.wireOp",EDGE,"E39.0.MirrorC")])],"isStart":false});var subQ1=makeQuery(id+"F2.opExtrude","SWEPT_FACE",FACE,{"disambiguationData":[OSD([sQuery(id+"F0.wireOp",EDGE,"E11.3")])]});Q1=makeQuery(id+"F3.boolean.opBoolean","SPLIT",EDGE,{"disambiguationData":[TD([makeQuery(id+"F3.opExtrude","SWEPT_FACE",FACE,{"disambiguationData":[OSD([sQuery(id+"F0.wireOp",EDGE,"E38.4.MirrorCS")])]})])],"derivedFrom":makeQuery(id+"F2.boolean.opBoolean","INTERSECT",EDGE,{"derivedFrom":[subQ0,subQ1]})});}
            var Q2;
            Q2=makeQuery(id+"F1.opExtrude","CAP_EDGE",EDGE,{"disambiguationData":[OSD([sQuery(id+"F0.wireOp",EDGE,"E38.13.MirrorCS")])],"isStart":false});
            var Q3;
            Q3=makeQuery(id+"F2.boolean.opBoolean","INTERSECT",EDGE,{"derivedFrom":[makeQuery(id+"F1.opExtrude","CAP_FACE",FACE,{"disambiguationData":[OSD([sQuery(id+"F0.wireOp",EDGE,"E0.rect.bottom"),sQuery(id+"F0.wireOp",EDGE,"E0.rect.top"),sQuery(id+"F0.wireOp",EDGE,"E0.rect.left"),sQuery(id+"F0.wireOp",EDGE,"E0.rect.right"),sQuery(id+"F0.wireOp",EDGE,"E1"),sQuery(id+"F0.wireOp",EDGE,"E2.0"),sQuery(id+"F0.wireOp",EDGE,"E7"),sQuery(id+"F0.wireOp",EDGE,"E10"),sQuery(id+"F0.wireOp",EDGE,"E12"),sQuery(id+"F0.wireOp",EDGE,"E14.0.MirrorCS"),sQuery(id+"F0.wireOp",EDGE,"E15.0.MirrorC"),sQuery(id+"F0.wireOp",EDGE,"E16.0.MirrorC"),sQuery(id+"F0.wireOp",EDGE,"E17.0.MirrorCS"),sQuery(id+"F0.wireOp",EDGE,"E18.0.MirrorCS"),sQuery(id+"F0.wireOp",EDGE,"E19.0.MirrorCS"),sQuery(id+"F0.wireOp",EDGE,"E20.0.MirrorC"),sQuery(id+"F0.wireOp",EDGE,"E21.0.MirrorC"),sQuery(id+"F0.wireOp",EDGE,"E22.0.MirrorCS"),sQuery(id+"F0.wireOp",EDGE,"E23.0.MirrorCS"),sQuery(id+"F0.wireOp",EDGE,"E24.0.MirrorC"),sQuery(id+"F0.wireOp",EDGE,"E25.0.MirrorC"),sQuery(id+"F0.wireOp",EDGE,"E29.0.MirrorC"),sQuery(id+"F0.wireOp",EDGE,"E38.6.MirrorC"),sQuery(id+"F0.wireOp",EDGE,"E39.0.MirrorC")])],"isStart":false}),makeQuery(id+"F2.opExtrude","SWEPT_FACE",FACE,{"disambiguationData":[OSD([sQuery(id+"F0.wireOp",EDGE,"E11.1")])]})]});
            var Q4;
            Q4=makeQuery(id+"F2.boolean.opBoolean","INTERSECT",EDGE,{"derivedFrom":[makeQuery(id+"F1.opExtrude","CAP_FACE",FACE,{"disambiguationData":[OSD([sQuery(id+"F0.wireOp",EDGE,"E0.rect.bottom"),sQuery(id+"F0.wireOp",EDGE,"E0.rect.top"),sQuery(id+"F0.wireOp",EDGE,"E0.rect.left"),sQuery(id+"F0.wireOp",EDGE,"E0.rect.right"),sQuery(id+"F0.wireOp",EDGE,"E1"),sQuery(id+"F0.wireOp",EDGE,"E2.0"),sQuery(id+"F0.wireOp",EDGE,"E7"),sQuery(id+"F0.wireOp",EDGE,"E10"),sQuery(id+"F0.wireOp",EDGE,"E12"),sQuery(id+"F0.wireOp",EDGE,"E14.0.MirrorCS"),sQuery(id+"F0.wireOp",EDGE,"E15.0.MirrorC"),sQuery(id+"F0.wireOp",EDGE,"E16.0.MirrorC"),sQuery(id+"F0.wireOp",EDGE,"E17.0.MirrorCS"),sQuery(id+"F0.wireOp",EDGE,"E18.0.MirrorCS"),sQuery(id+"F0.wireOp",EDGE,"E19.0.MirrorCS"),sQuery(id+"F0.wireOp",EDGE,"E20.0.MirrorC"),sQuery(id+"F0.wireOp",EDGE,"E21.0.MirrorC"),sQuery(id+"F0.wireOp",EDGE,"E22.0.MirrorCS"),sQuery(id+"F0.wireOp",EDGE,"E23.0.MirrorCS"),sQuery(id+"F0.wireOp",EDGE,"E24.0.MirrorC"),sQuery(id+"F0.wireOp",EDGE,"E25.0.MirrorC"),sQuery(id+"F0.wireOp",EDGE,"E29.0.MirrorC"),sQuery(id+"F0.wireOp",EDGE,"E38.6.MirrorC"),sQuery(id+"F0.wireOp",EDGE,"E39.0.MirrorC")])],"isStart":false}),makeQuery(id+"F2.opExtrude","SWEPT_FACE",FACE,{"disambiguationData":[OSD([sQuery(id+"F0.wireOp",EDGE,"E11.6")])]})]});
            var Q5;
            {var subQ0=sQuery(id+"F0.wireOp",EDGE,"E12");var subQ1=sQuery(id+"F0.wireOp",EDGE,"E29.0.MirrorC");var subQ2=sQuery(id+"F0.wireOp",EDGE,"E38.6.MirrorC");var subQ3=sQuery(id+"F0.wireOp",EDGE,"E39.0.MirrorC");Q5=makeQuery(id+"F3.boolean.opBoolean","INTERSECT",EDGE,{"derivedFrom":[makeQuery(id+"F2.boolean.opBoolean","SPLIT",FACE,{"disambiguationData":[TD([makeQuery(id+"F1.opExtrude","SWEPT_FACE",FACE,{"disambiguationData":[OSD([subQ0])]})])],"derivedFrom":makeQuery(id+"F1.opExtrude","CAP_FACE",FACE,{"disambiguationData":[OSD([sQuery(id+"F0.wireOp",EDGE,"E0.rect.bottom"),sQuery(id+"F0.wireOp",EDGE,"E0.rect.top"),sQuery(id+"F0.wireOp",EDGE,"E0.rect.left"),sQuery(id+"F0.wireOp",EDGE,"E0.rect.right"),sQuery(id+"F0.wireOp",EDGE,"E1"),sQuery(id+"F0.wireOp",EDGE,"E2.0"),sQuery(id+"F0.wireOp",EDGE,"E7"),sQuery(id+"F0.wireOp",EDGE,"E10"),subQ0,sQuery(id+"F0.wireOp",EDGE,"E14.0.MirrorCS"),sQuery(id+"F0.wireOp",EDGE,"E15.0.MirrorC"),sQuery(id+"F0.wireOp",EDGE,"E16.0.MirrorC"),sQuery(id+"F0.wireOp",EDGE,"E17.0.MirrorCS"),sQuery(id+"F0.wireOp",EDGE,"E18.0.MirrorCS"),sQuery(id+"F0.wireOp",EDGE,"E19.0.MirrorCS"),sQuery(id+"F0.wireOp",EDGE,"E20.0.MirrorC"),sQuery(id+"F0.wireOp",EDGE,"E21.0.MirrorC"),sQuery(id+"F0.wireOp",EDGE,"E22.0.MirrorCS"),sQuery(id+"F0.wireOp",EDGE,"E23.0.MirrorCS"),sQuery(id+"F0.wireOp",EDGE,"E24.0.MirrorC"),sQuery(id+"F0.wireOp",EDGE,"E25.0.MirrorC"),subQ1,subQ2,subQ3])],"isStart":false})}),makeQuery(id+"F3.opExtrude","SWEPT_FACE",FACE,{"disambiguationData":[OSD([sQuery(id+"F0.wireOp",EDGE,"E13.0")])]})]});}
            var Q6;
            {var subQ0=makeQuery(id+"F1.opExtrude","CAP_FACE",FACE,{"disambiguationData":[OSD([sQuery(id+"F0.wireOp",EDGE,"E0.rect.bottom"),sQuery(id+"F0.wireOp",EDGE,"E0.rect.top"),sQuery(id+"F0.wireOp",EDGE,"E0.rect.left"),sQuery(id+"F0.wireOp",EDGE,"E0.rect.right"),sQuery(id+"F0.wireOp",EDGE,"E1"),sQuery(id+"F0.wireOp",EDGE,"E2.0"),sQuery(id+"F0.wireOp",EDGE,"E7"),sQuery(id+"F0.wireOp",EDGE,"E10"),sQuery(id+"F0.wireOp",EDGE,"E12"),sQuery(id+"F0.wireOp",EDGE,"E14.0.MirrorCS"),sQuery(id+"F0.wireOp",EDGE,"E15.0.MirrorC"),sQuery(id+"F0.wireOp",EDGE,"E16.0.MirrorC"),sQuery(id+"F0.wireOp",EDGE,"E17.0.MirrorCS"),sQuery(id+"F0.wireOp",EDGE,"E18.0.MirrorCS"),sQuery(id+"F0.wireOp",EDGE,"E19.0.MirrorCS"),sQuery(id+"F0.wireOp",EDGE,"E20.0.MirrorC"),sQuery(id+"F0.wireOp",EDGE,"E21.0.MirrorC"),sQuery(id+"F0.wireOp",EDGE,"E22.0.MirrorCS"),sQuery(id+"F0.wireOp",EDGE,"E23.0.MirrorCS"),sQuery(id+"F0.wireOp",EDGE,"E24.0.MirrorC"),sQuery(id+"F0.wireOp",EDGE,"E25.0.MirrorC"),sQuery(id+"F0.wireOp",EDGE,"E29.0.MirrorC"),sQuery(id+"F0.wireOp",EDGE,"E38.6.MirrorC"),sQuery(id+"F0.wireOp",EDGE,"E39.0.MirrorC")])],"isStart":false});var subQ1=makeQuery(id+"F2.opExtrude","SWEPT_FACE",FACE,{"disambiguationData":[OSD([sQuery(id+"F0.wireOp",EDGE,"E11.5")])]});Q6=makeQuery(id+"F3.boolean.opBoolean","SPLIT",EDGE,{"disambiguationData":[TD([makeQuery(id+"F3.opExtrude","SWEPT_FACE",FACE,{"disambiguationData":[OSD([sQuery(id+"F0.wireOp",EDGE,"E28")])]})])],"derivedFrom":makeQuery(id+"F2.boolean.opBoolean","INTERSECT",EDGE,{"derivedFrom":[subQ0,subQ1]})});}
            var Q7;
            Q7=makeQuery(id+"F1.opExtrude","CAP_EDGE",EDGE,{"disambiguationData":[OSD([sQuery(id+"F0.wireOp",EDGE,"E33.0.MirrorCS")])],"isStart":false});
            var Q8;
            {var subQ0=sQuery(id+"F0.wireOp",EDGE,"E12");var subQ1=sQuery(id+"F0.wireOp",EDGE,"E29.0.MirrorC");var subQ2=sQuery(id+"F0.wireOp",EDGE,"E38.6.MirrorC");var subQ3=sQuery(id+"F0.wireOp",EDGE,"E39.0.MirrorC");Q8=makeQuery(id+"F3.boolean.opBoolean","INTERSECT",EDGE,{"derivedFrom":[makeQuery(id+"F2.boolean.opBoolean","SPLIT",FACE,{"disambiguationData":[TD([makeQuery(id+"F1.opExtrude","SWEPT_FACE",FACE,{"disambiguationData":[OSD([subQ0])]})])],"derivedFrom":makeQuery(id+"F1.opExtrude","CAP_FACE",FACE,{"disambiguationData":[OSD([sQuery(id+"F0.wireOp",EDGE,"E0.rect.bottom"),sQuery(id+"F0.wireOp",EDGE,"E0.rect.top"),sQuery(id+"F0.wireOp",EDGE,"E0.rect.left"),sQuery(id+"F0.wireOp",EDGE,"E0.rect.right"),sQuery(id+"F0.wireOp",EDGE,"E1"),sQuery(id+"F0.wireOp",EDGE,"E2.0"),sQuery(id+"F0.wireOp",EDGE,"E7"),sQuery(id+"F0.wireOp",EDGE,"E10"),subQ0,sQuery(id+"F0.wireOp",EDGE,"E14.0.MirrorCS"),sQuery(id+"F0.wireOp",EDGE,"E15.0.MirrorC"),sQuery(id+"F0.wireOp",EDGE,"E16.0.MirrorC"),sQuery(id+"F0.wireOp",EDGE,"E17.0.MirrorCS"),sQuery(id+"F0.wireOp",EDGE,"E18.0.MirrorCS"),sQuery(id+"F0.wireOp",EDGE,"E19.0.MirrorCS"),sQuery(id+"F0.wireOp",EDGE,"E20.0.MirrorC"),sQuery(id+"F0.wireOp",EDGE,"E21.0.MirrorC"),sQuery(id+"F0.wireOp",EDGE,"E22.0.MirrorCS"),sQuery(id+"F0.wireOp",EDGE,"E23.0.MirrorCS"),sQuery(id+"F0.wireOp",EDGE,"E24.0.MirrorC"),sQuery(id+"F0.wireOp",EDGE,"E25.0.MirrorC"),subQ1,subQ2,subQ3])],"isStart":false})}),makeQuery(id+"F3.opExtrude","SWEPT_FACE",FACE,{"disambiguationData":[OSD([sQuery(id+"F0.wireOp",EDGE,"E38.3.MirrorCS")])]})]});}
            var Q9;
            {var subQ0=sQuery(id+"F0.wireOp",EDGE,"E12");var subQ1=sQuery(id+"F0.wireOp",EDGE,"E29.0.MirrorC");var subQ2=sQuery(id+"F0.wireOp",EDGE,"E38.6.MirrorC");var subQ3=sQuery(id+"F0.wireOp",EDGE,"E39.0.MirrorC");Q9=makeQuery(id+"F3.boolean.opBoolean","INTERSECT",EDGE,{"derivedFrom":[makeQuery(id+"F2.boolean.opBoolean","SPLIT",FACE,{"disambiguationData":[TD([makeQuery(id+"F1.opExtrude","SWEPT_FACE",FACE,{"disambiguationData":[OSD([subQ0])]})])],"derivedFrom":makeQuery(id+"F1.opExtrude","CAP_FACE",FACE,{"disambiguationData":[OSD([sQuery(id+"F0.wireOp",EDGE,"E0.rect.bottom"),sQuery(id+"F0.wireOp",EDGE,"E0.rect.top"),sQuery(id+"F0.wireOp",EDGE,"E0.rect.left"),sQuery(id+"F0.wireOp",EDGE,"E0.rect.right"),sQuery(id+"F0.wireOp",EDGE,"E1"),sQuery(id+"F0.wireOp",EDGE,"E2.0"),sQuery(id+"F0.wireOp",EDGE,"E7"),sQuery(id+"F0.wireOp",EDGE,"E10"),subQ0,sQuery(id+"F0.wireOp",EDGE,"E14.0.MirrorCS"),sQuery(id+"F0.wireOp",EDGE,"E15.0.MirrorC"),sQuery(id+"F0.wireOp",EDGE,"E16.0.MirrorC"),sQuery(id+"F0.wireOp",EDGE,"E17.0.MirrorCS"),sQuery(id+"F0.wireOp",EDGE,"E18.0.MirrorCS"),sQuery(id+"F0.wireOp",EDGE,"E19.0.MirrorCS"),sQuery(id+"F0.wireOp",EDGE,"E20.0.MirrorC"),sQuery(id+"F0.wireOp",EDGE,"E21.0.MirrorC"),sQuery(id+"F0.wireOp",EDGE,"E22.0.MirrorCS"),sQuery(id+"F0.wireOp",EDGE,"E23.0.MirrorCS"),sQuery(id+"F0.wireOp",EDGE,"E24.0.MirrorC"),sQuery(id+"F0.wireOp",EDGE,"E25.0.MirrorC"),subQ1,subQ2,subQ3])],"isStart":false})}),makeQuery(id+"F3.opExtrude","SWEPT_FACE",FACE,{"disambiguationData":[OSD([sQuery(id+"F0.wireOp",EDGE,"E38.9.MirrorCS")])]})]});}
            var Q10;
            {var subQ0=sQuery(id+"F0.wireOp",EDGE,"E12");var subQ1=sQuery(id+"F0.wireOp",EDGE,"E29.0.MirrorC");var subQ2=sQuery(id+"F0.wireOp",EDGE,"E38.6.MirrorC");var subQ3=sQuery(id+"F0.wireOp",EDGE,"E39.0.MirrorC");Q10=makeQuery(id+"F3.boolean.opBoolean","INTERSECT",EDGE,{"derivedFrom":[makeQuery(id+"F2.boolean.opBoolean","SPLIT",FACE,{"disambiguationData":[TD([makeQuery(id+"F1.opExtrude","SWEPT_FACE",FACE,{"disambiguationData":[OSD([subQ0])]})])],"derivedFrom":makeQuery(id+"F1.opExtrude","CAP_FACE",FACE,{"disambiguationData":[OSD([sQuery(id+"F0.wireOp",EDGE,"E0.rect.bottom"),sQuery(id+"F0.wireOp",EDGE,"E0.rect.top"),sQuery(id+"F0.wireOp",EDGE,"E0.rect.left"),sQuery(id+"F0.wireOp",EDGE,"E0.rect.right"),sQuery(id+"F0.wireOp",EDGE,"E1"),sQuery(id+"F0.wireOp",EDGE,"E2.0"),sQuery(id+"F0.wireOp",EDGE,"E7"),sQuery(id+"F0.wireOp",EDGE,"E10"),subQ0,sQuery(id+"F0.wireOp",EDGE,"E14.0.MirrorCS"),sQuery(id+"F0.wireOp",EDGE,"E15.0.MirrorC"),sQuery(id+"F0.wireOp",EDGE,"E16.0.MirrorC"),sQuery(id+"F0.wireOp",EDGE,"E17.0.MirrorCS"),sQuery(id+"F0.wireOp",EDGE,"E18.0.MirrorCS"),sQuery(id+"F0.wireOp",EDGE,"E19.0.MirrorCS"),sQuery(id+"F0.wireOp",EDGE,"E20.0.MirrorC"),sQuery(id+"F0.wireOp",EDGE,"E21.0.MirrorC"),sQuery(id+"F0.wireOp",EDGE,"E22.0.MirrorCS"),sQuery(id+"F0.wireOp",EDGE,"E23.0.MirrorCS"),sQuery(id+"F0.wireOp",EDGE,"E24.0.MirrorC"),sQuery(id+"F0.wireOp",EDGE,"E25.0.MirrorC"),subQ1,subQ2,subQ3])],"isStart":false})}),makeQuery(id+"F3.opExtrude","SWEPT_FACE",FACE,{"disambiguationData":[OSD([sQuery(id+"F0.wireOp",EDGE,"E33.0.MirrorCS")])]})]});}
            fillet(context, id + "F11", {"entities" : qUnion([Q0, Q1, Q2, Q3, Q4, Q5, Q6, Q7, Q8, Q9, Q10]), "radius" : 1 * mm, "tangentPropagation" : true, "allowEdgeOverflow" : false});
        }
        {
            var Q0;
            Q0=makeQuery(id+"F0.imprint","IMPRINT",FACE,{"disambiguationData":[TD([[makeQuery(id+"F0.imprint","IMPRINT",EDGE,{"derivedFrom":sQuery(id+"F0.wireOp",EDGE,"E38.7.MirrorCS")}),-1.0]])]});
            var Q1;
            {var subQ3=sQuery(id+"F0.wireOp",EDGE,"E11.4");Q1=makeQuery(id+"F0.imprint","IMPRINT",FACE,{"disambiguationData":[TD([[makeQuery(id+"F0.imprint","IMPRINT",EDGE,{"derivedFrom":subQ3}),1.0]])]});}
            var Q2;
            Q2=makeQuery(id+"F0.imprint","IMPRINT",FACE,{"disambiguationData":[TD([[makeQuery(id+"F0.imprint","IMPRINT",EDGE,{"derivedFrom":sQuery(id+"F0.wireOp",EDGE,"E0.rect.right")}),1.0]])]});
            var Q3;
            Q3=makeQuery(id+"F0.imprint","IMPRINT",FACE,{"disambiguationData":[TD([[makeQuery(id+"F0.imprint","IMPRINT",EDGE,{"derivedFrom":sQuery(id+"F0.wireOp",EDGE,"E13.0")}),-1.0]])]});
            var Q4;
            Q4=makeQuery(id+"F0.imprint","IMPRINT",FACE,{"disambiguationData":[TD([[makeQuery(id+"F0.imprint","IMPRINT",EDGE,{"derivedFrom":sQuery(id+"F0.wireOp",EDGE,"E38.0.MirrorCS")}),1.0]])]});
            var Q5;
            {var subQ3=sQuery(id+"F0.wireOp",EDGE,"E11.2");Q5=makeQuery(id+"F0.imprint","IMPRINT",FACE,{"disambiguationData":[TD([[makeQuery(id+"F0.imprint","IMPRINT",EDGE,{"derivedFrom":subQ3}),1.0]])]});}
            var Q6;
            Q6=makeQuery(id+"F0.imprint","IMPRINT",FACE,{"disambiguationData":[TD([[makeQuery(id+"F0.imprint","IMPRINT",EDGE,{"derivedFrom":sQuery(id+"F0.wireOp",EDGE,"E12")}),-1.0]])]});
            var Q7;
            {var subQ3=sQuery(id+"F0.wireOp",EDGE,"E11.0");Q7=makeQuery(id+"F0.imprint","IMPRINT",FACE,{"disambiguationData":[TD([[makeQuery(id+"F0.imprint","IMPRINT",EDGE,{"derivedFrom":subQ3}),1.0]])]});}
            var Q8;
            Q8=makeQuery(id+"F0.imprint","IMPRINT",FACE,{"disambiguationData":[TD([[makeQuery(id+"F0.imprint","IMPRINT",EDGE,{"derivedFrom":sQuery(id+"F0.wireOp",EDGE,"E38.6.MirrorC")}),-1.0]])]});
            var Q9;
            Q9=makeQuery(id+"F0.imprint","IMPRINT",FACE,{"disambiguationData":[TD([[makeQuery(id+"F0.imprint","IMPRINT",EDGE,{"derivedFrom":sQuery(id+"F0.wireOp",EDGE,"E39.0.MirrorC")}),1.0]])]});
            var Q10;
            Q10=makeQuery(id+"F0.imprint","IMPRINT",FACE,{"disambiguationData":[TD([[makeQuery(id+"F0.imprint","IMPRINT",EDGE,{"derivedFrom":sQuery(id+"F0.wireOp",EDGE,"E29.0.MirrorC")}),1.0]])]});
            var Q11;
            Q11=makeQuery(id+"F0.imprint","IMPRINT",FACE,{"disambiguationData":[TD([[makeQuery(id+"F0.imprint","IMPRINT",EDGE,{"derivedFrom":sQuery(id+"F0.wireOp",EDGE,"E29.0.MirrorC")}),-1.0]])]});
            var Q12;
            Q12=makeQuery(id+"F0.imprint","IMPRINT",FACE,{"disambiguationData":[TD([[makeQuery(id+"F0.imprint","IMPRINT",EDGE,{"derivedFrom":sQuery(id+"F0.wireOp",EDGE,"E29.0.MirrorC")}),1.0]])]});
            var Q13;
            Q13=makeQuery(id+"F0.imprint","IMPRINT",FACE,{"disambiguationData":[TD([[makeQuery(id+"F0.imprint","IMPRINT",EDGE,{"derivedFrom":sQuery(id+"F0.wireOp",EDGE,"E38.6.MirrorC")}),-1.0]])]});
            var Q14;
            Q14=makeQuery(id+"F0.imprint","IMPRINT",FACE,{"disambiguationData":[TD([[makeQuery(id+"F0.imprint","IMPRINT",EDGE,{"derivedFrom":sQuery(id+"F0.wireOp",EDGE,"E29.0.MirrorC")}),1.0]])]});
            var Q15;
            {var subQ2=sQuery(id+"F0.wireOp",EDGE,"E11.7");Q15=makeQuery(id+"F0.imprint","IMPRINT",FACE,{"disambiguationData":[TD([[makeQuery(id+"F0.imprint","IMPRINT",EDGE,{"derivedFrom":subQ2}),1.0]])]});}
            var Q16;
            Q16=makeQuery(id+"F0.imprint","IMPRINT",FACE,{"disambiguationData":[TD([[makeQuery(id+"F0.imprint","IMPRINT",EDGE,{"derivedFrom":sQuery(id+"F0.wireOp",EDGE,"E29.0.MirrorC")}),-1.0]])]});
            var Q17;
            Q17=makeQuery(id+"F0.imprint","IMPRINT",FACE,{"disambiguationData":[TD([[makeQuery(id+"F0.imprint","IMPRINT",EDGE,{"derivedFrom":sQuery(id+"F0.wireOp",EDGE,"E39.0.MirrorC")}),1.0]])]});
            var Q18;
            Q18=makeQuery(id+"F0.imprint","IMPRINT",FACE,{"disambiguationData":[TD([[makeQuery(id+"F0.imprint","IMPRINT",EDGE,{"derivedFrom":sQuery(id+"F0.wireOp",EDGE,"E12")}),1.0]])]});
            extrude(context, id + "F12", {"entities" : qUnion([Q0, Q1, Q2, Q3, Q4, Q5, Q6, Q7, Q8, Q9, Q10, Q11, Q12, Q13, Q14, Q15, Q16, Q17, Q18]), "depth" : 4 * mm});
        }
        {
            var Q0;
            Q0=makeQuery(id+"F12.opExtrude","CAP_FACE",FACE,{"disambiguationData":[OSD([sQuery(id+"F0.wireOp",EDGE,"E0.rect.bottom"),sQuery(id+"F0.wireOp",EDGE,"E0.rect.top"),sQuery(id+"F0.wireOp",EDGE,"E0.rect.right"),sQuery(id+"F0.wireOp",EDGE,"E3.filletArc"),sQuery(id+"F0.wireOp",EDGE,"E4.filletArc"),sQuery(id+"F0.wireOp",EDGE,"E5.filletArc"),sQuery(id+"F0.wireOp",EDGE,"E6.filletArc"),sQuery(id+"F0.wireOp",EDGE,"E10")])],"isStart":true});
            shell(context, id + "F13", {"entities" : qUnion([Q0]), "thickness" : 1.2 * mm});
        }
        {
            var Q0;
            Q0=makeQuery(id+"F0.imprint","IMPRINT",FACE,{"disambiguationData":[TD([[makeQuery(id+"F0.imprint","IMPRINT",EDGE,{"derivedFrom":sQuery(id+"F0.wireOp",EDGE,"E0.rect.right")}),1.0]])]});
            var sketch = newSketch(context, id + "F14", { "sketchPlane" : qUnion([Q0])});
            skLineSegment(sketch, "E48.bottom", {"start": v(-30.25, 18.05) * mm, "end": v(-21.05, 18.05) * mm});
            skLineSegment(sketch, "E48.top", {"start": v(-30.25, -6.95) * mm, "end": v(-21.05, -6.95) * mm});
            skLineSegment(sketch, "E48.left", {"start": v(-30.25, 18.05) * mm, "end": v(-30.25, -6.95) * mm});
            skLineSegment(sketch, "E48.right", {"start": v(-21.05, 18.05) * mm, "end": v(-21.05, -6.95) * mm});
            skLineSegment(sketch, "E49.bottom", {"start": v(-17.5, -27.25) * mm, "end": v(17.5, -27.25) * mm});
            skLineSegment(sketch, "E49.top", {"start": v(-17.5, -15.75) * mm, "end": v(17.5, -15.75) * mm});
            skLineSegment(sketch, "E49.left", {"start": v(-17.5, -27.25) * mm, "end": v(-17.5, -15.75) * mm});
            skLineSegment(sketch, "E49.right", {"start": v(17.5, -27.25) * mm, "end": v(17.5, -15.75) * mm});
            skLineSegment(sketch, "E50.bottom", {"start": v(30.25, 5.05) * mm, "end": v(21.05, 5.05) * mm});
            skLineSegment(sketch, "E50.top", {"start": v(30.25, -12.45) * mm, "end": v(21.05, -12.45) * mm});
            skLineSegment(sketch, "E50.left", {"start": v(30.25, 5.05) * mm, "end": v(30.25, -12.45) * mm});
            skLineSegment(sketch, "E50.right", {"start": v(21.05, 5.05) * mm, "end": v(21.05, -12.45) * mm});
            skLineSegment(sketch, "E51.rect.bottom", {"start": v(16.5, 15.05) * mm, "end": v(-16.5, 15.05) * mm});
            skLineSegment(sketch, "E51.rect.top", {"start": v(16.5, -8.25) * mm, "end": v(-16.5, -8.25) * mm});
            skLineSegment(sketch, "E51.rect.left", {"start": v(16.5, 15.05) * mm, "end": v(16.5, -8.25) * mm});
            skLineSegment(sketch, "E51.rect.right", {"start": v(-16.5, 15.05) * mm, "end": v(-16.5, -8.25) * mm});
            skPoint(sketch, "E52", {"position": v(0, -8.25) * mm});
            skLineSegment(sketch, "E53.0", {"start": v(-17.7, 16.25) * mm, "end": v(-17.7, -9.45) * mm});
            skLineSegment(sketch, "E53.1", {"start": v(17.7, 16.25) * mm, "end": v(-17.7, 16.25) * mm});
            skLineSegment(sketch, "E53.2", {"start": v(17.7, 16.25) * mm, "end": v(17.7, -9.45) * mm});
            skLineSegment(sketch, "E53.3", {"start": v(17.7, -9.45) * mm, "end": v(-17.7, -9.45) * mm});
            skSolve(sketch);
        }
        {
            var Q0;
            {var subQ6=sQuery(id+"F14.wireOp",EDGE,"E48.right");Q0=makeQuery(id+"F14.imprint","IMPRINT",FACE,{"disambiguationData":[TD([[makeQuery(id+"F14.imprint","IMPRINT",EDGE,{"derivedFrom":subQ6}),-1.0]])]});}
            var Q1;
            {var subQ6=sQuery(id+"F14.wireOp",EDGE,"E50.right");Q1=makeQuery(id+"F14.imprint","IMPRINT",FACE,{"disambiguationData":[TD([[makeQuery(id+"F14.imprint","IMPRINT",EDGE,{"derivedFrom":subQ6}),1.0]])]});}
            var Q2;
            {var subQ6=sQuery(id+"F14.wireOp",EDGE,"E49.top");Q2=makeQuery(id+"F14.imprint","IMPRINT",FACE,{"disambiguationData":[TD([[makeQuery(id+"F14.imprint","IMPRINT",EDGE,{"derivedFrom":subQ6}),-1.0]])]});}
            var Q3;
            Q3=makeQuery(id+"F14.imprint","IMPRINT",FACE,{"disambiguationData":[TD([[makeQuery(id+"F14.imprint","IMPRINT",EDGE,{"derivedFrom":sQuery(id+"F14.wireOp",EDGE,"E51.rect.bottom")}),1.0]])]});
            var Q4;
            {var subQ8=sQuery(id+"F14.wireOp",EDGE,"E49.bottom");Q4=makeQuery(id+"F14.imprint","IMPRINT",FACE,{"disambiguationData":[TD([[makeQuery(id+"F14.imprint","IMPRINT",EDGE,{"derivedFrom":subQ8}),-1.0]])]});}
            var Q5;
            Q5=makeQuery(id+"F12.opExtrude","CAP_FACE",FACE,{"disambiguationData":[OSD([sQuery(id+"F0.wireOp",EDGE,"E0.rect.bottom"),sQuery(id+"F0.wireOp",EDGE,"E0.rect.top"),sQuery(id+"F0.wireOp",EDGE,"E0.rect.right"),sQuery(id+"F0.wireOp",EDGE,"E3.filletArc"),sQuery(id+"F0.wireOp",EDGE,"E4.filletArc"),sQuery(id+"F0.wireOp",EDGE,"E5.filletArc"),sQuery(id+"F0.wireOp",EDGE,"E6.filletArc"),sQuery(id+"F0.wireOp",EDGE,"E10")])],"isStart":false});
            extrude(context, id + "F15", {"entities" : qUnion([Q0, Q1, Q2, Q3, Q4]), "operationType" : NewBodyOperationType.REMOVE, "endBound" : BoundingType.THROUGH_ALL, "endBoundEntity" : qUnion([Q5]), "depth" : 25 * mm});
        }
        {
            var Q0;
            Q0=makeQuery(id+"F12.opExtrude","CAP_EDGE",EDGE,{"disambiguationData":[OSD([sQuery(id+"F0.wireOp",EDGE,"E3.filletArc")])],"isStart":false});
            chamfer(context, id + "F16", {"entities" : qUnion([Q0]), "width" : 1.2 * mm, "tangentPropagation" : true});
        }
        {
            var Q0;
            {var subQ0=sQuery(id+"F0.wireOp",EDGE,"E0.rect.top");var subQ1=sQuery(id+"F0.wireOp",EDGE,"E5.filletArc");Q0=makeQuery(id+"F15.boolean.opBoolean","SPLIT",EDGE,{"disambiguationData":[TD([makeQuery(id+"F13.opShell","OFFSET_FACE",FACE,{"disambiguationData":[OSD([subQ1])]})])],"derivedFrom":makeQuery(id+"F13.opShell","OFFSET_EDGE",EDGE,{"disambiguationData":[OSD([subQ0]),TDD([makeQuery(id+"F12.opExtrude","CAP_EDGE",EDGE,{"disambiguationData":[OSD([subQ0])],"isStart":false})])]})});}
            var Q1;
            {var subQ0=sQuery(id+"F0.wireOp",EDGE,"E10");var subQ1=sQuery(id+"F0.wireOp",EDGE,"E3.filletArc");Q1=makeQuery(id+"F15.boolean.opBoolean","SPLIT",EDGE,{"disambiguationData":[TD([makeQuery(id+"F13.opShell","OFFSET_FACE",FACE,{"disambiguationData":[OSD([subQ1])]})])],"derivedFrom":makeQuery(id+"F13.opShell","OFFSET_EDGE",EDGE,{"disambiguationData":[OSD([subQ0]),TDD([makeQuery(id+"F12.opExtrude","CAP_EDGE",EDGE,{"disambiguationData":[OSD([subQ0])],"isStart":false})])]})});}
            var Q2;
            {var subQ0=sQuery(id+"F0.wireOp",EDGE,"E0.rect.top");var subQ1=sQuery(id+"F0.wireOp",EDGE,"E6.filletArc");Q2=makeQuery(id+"F15.boolean.opBoolean","SPLIT",EDGE,{"disambiguationData":[TD([makeQuery(id+"F13.opShell","OFFSET_FACE",FACE,{"disambiguationData":[OSD([subQ1])]})])],"derivedFrom":makeQuery(id+"F13.opShell","OFFSET_EDGE",EDGE,{"disambiguationData":[OSD([subQ0]),TDD([makeQuery(id+"F12.opExtrude","CAP_EDGE",EDGE,{"disambiguationData":[OSD([subQ0])],"isStart":false})])]})});}
            var Q3;
            Q3=makeQuery(id+"F15.boolean.opBoolean","COPY",EDGE,{"derivedFrom":makeQuery(id+"F15.opExtrude","SWEPT_EDGE",EDGE,{"disambiguationData":[OSD([sQuery(id+"F14.wireOp",EDGE,"E49.top"),sQuery(id+"F14.wireOp",EDGE,"E49.left")])]})});
            var Q4;
            Q4=makeQuery(id+"F15.boolean.opBoolean","COPY",EDGE,{"derivedFrom":makeQuery(id+"F15.opExtrude","SWEPT_EDGE",EDGE,{"disambiguationData":[OSD([sQuery(id+"F14.wireOp",EDGE,"E49.top"),sQuery(id+"F14.wireOp",EDGE,"E49.right")])]})});
            fillet(context, id + "F17", {"entities" : qUnion([Q0, Q1, Q2, Q3, Q4]), "radius" : 1 * mm, "tangentPropagation" : true, "allowEdgeOverflow" : false});
        }
        {
            var Q0;
            {var subQ3=sQuery(id+"F0.wireOp",EDGE,"E11.0");Q0=makeQuery(id+"F0.imprint","IMPRINT",FACE,{"disambiguationData":[TD([[makeQuery(id+"F0.imprint","IMPRINT",EDGE,{"derivedFrom":subQ3}),1.0]])]});}
            var Q1;
            {var subQ2=sQuery(id+"F0.wireOp",EDGE,"E11.7");Q1=makeQuery(id+"F0.imprint","IMPRINT",FACE,{"disambiguationData":[TD([[makeQuery(id+"F0.imprint","IMPRINT",EDGE,{"derivedFrom":subQ2}),1.0]])]});}
            var Q2;
            {var subQ3=sQuery(id+"F0.wireOp",EDGE,"E11.4");Q2=makeQuery(id+"F0.imprint","IMPRINT",FACE,{"disambiguationData":[TD([[makeQuery(id+"F0.imprint","IMPRINT",EDGE,{"derivedFrom":subQ3}),1.0]])]});}
            var Q3;
            {var subQ3=sQuery(id+"F0.wireOp",EDGE,"E11.2");Q3=makeQuery(id+"F0.imprint","IMPRINT",FACE,{"disambiguationData":[TD([[makeQuery(id+"F0.imprint","IMPRINT",EDGE,{"derivedFrom":subQ3}),1.0]])]});}
            var Q4;
            Q4=makeQuery(id+"F1.opExtrude","SWEPT_BODY",BODY,{"disambiguationData":[OSD([sQuery(id+"F0.wireOp",EDGE,"E0.rect.bottom"),sQuery(id+"F0.wireOp",EDGE,"E0.rect.top"),sQuery(id+"F0.wireOp",EDGE,"E0.rect.left"),sQuery(id+"F0.wireOp",EDGE,"E0.rect.right"),sQuery(id+"F0.wireOp",EDGE,"E1"),sQuery(id+"F0.wireOp",EDGE,"E2.0"),sQuery(id+"F0.wireOp",EDGE,"E7"),sQuery(id+"F0.wireOp",EDGE,"E10"),sQuery(id+"F0.wireOp",EDGE,"E12"),sQuery(id+"F0.wireOp",EDGE,"E14.0.MirrorCS"),sQuery(id+"F0.wireOp",EDGE,"E15.0.MirrorC"),sQuery(id+"F0.wireOp",EDGE,"E16.0.MirrorC"),sQuery(id+"F0.wireOp",EDGE,"E17.0.MirrorCS"),sQuery(id+"F0.wireOp",EDGE,"E18.0.MirrorCS"),sQuery(id+"F0.wireOp",EDGE,"E19.0.MirrorCS"),sQuery(id+"F0.wireOp",EDGE,"E20.0.MirrorC"),sQuery(id+"F0.wireOp",EDGE,"E21.0.MirrorC"),sQuery(id+"F0.wireOp",EDGE,"E22.0.MirrorCS"),sQuery(id+"F0.wireOp",EDGE,"E23.0.MirrorCS"),sQuery(id+"F0.wireOp",EDGE,"E24.0.MirrorC"),sQuery(id+"F0.wireOp",EDGE,"E25.0.MirrorC"),sQuery(id+"F0.wireOp",EDGE,"E29.0.MirrorC"),sQuery(id+"F0.wireOp",EDGE,"E38.6.MirrorC"),sQuery(id+"F0.wireOp",EDGE,"E39.0.MirrorC")])]});
            extrude(context, id + "F18", {"entities" : qUnion([Q0, Q1, Q2, Q3]), "operationType" : NewBodyOperationType.ADD, "endBound" : BoundingType.SYMMETRIC, "oppositeDirection" : true, "endBoundEntity" : qUnion([Q4]), "depth" : 8 * mm});
        }
    });
